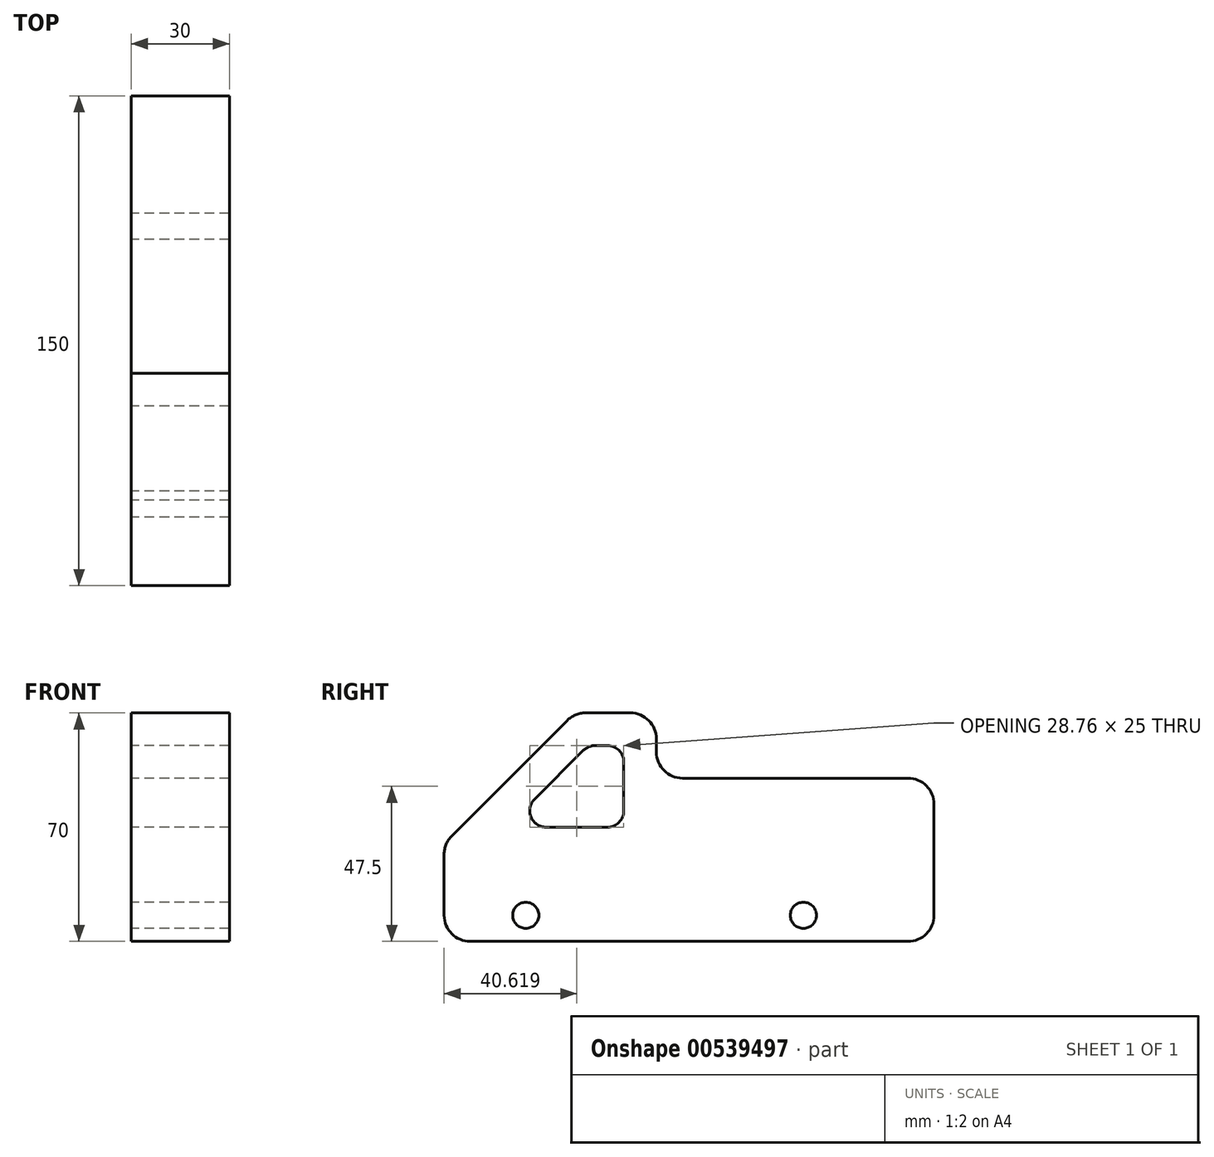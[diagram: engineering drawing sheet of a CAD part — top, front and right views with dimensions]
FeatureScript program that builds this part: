
annotation { "Feature Type Name" : "Feature", "Feature Type Description" : "" }
export const myFeature = defineFeature(function(context is Context, id is Id, definition is map)
    precondition{}
    {
        {
            var Q0;
            Q0=qCreatedBy(makeId("Right.planeOp"),FACE);
            var sketch = newSketch(context, id + "F0", { "sketchPlane" : qUnion([Q0])});
            skLineSegment(sketch, "E0", {"start": v(0, 0) * mm, "end": v(0, 30) * mm});
            skLineSegment(sketch, "E1", {"start": v(0, 30) * mm, "end": v(40, 70) * mm});
            skLineSegment(sketch, "E2", {"start": v(40, 70) * mm, "end": v(65, 70) * mm});
            skLineSegment(sketch, "E3", {"start": v(65, 70) * mm, "end": v(65, 50) * mm});
            skLineSegment(sketch, "E4", {"start": v(65, 50) * mm, "end": v(150, 50) * mm});
            skLineSegment(sketch, "E5", {"start": v(150, 50) * mm, "end": v(150, 0) * mm});
            skLineSegment(sketch, "E6", {"start": v(150, 0) * mm, "end": v(0, 0) * mm});
            skLineSegment(sketch, "E7.0", {"start": v(55, 60) * mm, "end": v(55, 35) * mm});
            skLineSegment(sketch, "E7.1", {"start": v(44.14, 60) * mm, "end": v(55, 60) * mm});
            skLineSegment(sketch, "E7.2", {"start": v(19.14, 35) * mm, "end": v(44.14, 60) * mm});
            skLineSegment(sketch, "E8", {"start": v(19.14, 35) * mm, "end": v(55, 35) * mm});
            skCircle(sketch, "E9", {"center": v(25, 8) * mm, "radius": 4 * mm});
            skCircle(sketch, "E10", {"center": v(110, 8) * mm, "radius": 4 * mm});
            skSolve(sketch);
        }
        {
            var Q0;
            Q0 = qSketchRegion(id + "F0", true);
            extrude(context, id + "F1", {"entities" : qUnion([Q0]), "endBound" : BoundingType.SYMMETRIC, "depth" : 30 * mm, "offsetDistance" : 25 * mm});
        }
        {
            var Q0;
            Q0=makeQuery(id+"F1.opExtrude","SWEPT_EDGE",EDGE,{"disambiguationData":[OSD([sQuery(id+"F0.wireOp",EDGE,"E1"),sQuery(id+"F0.wireOp",EDGE,"E2")])]});
            var Q1;
            Q1=makeQuery(id+"F1.opExtrude","SWEPT_EDGE",EDGE,{"disambiguationData":[OSD([sQuery(id+"F0.wireOp",EDGE,"E0"),sQuery(id+"F0.wireOp",EDGE,"E1")])]});
            var Q2;
            Q2=makeQuery(id+"F1.opExtrude","SWEPT_EDGE",EDGE,{"disambiguationData":[OSD([sQuery(id+"F0.wireOp",EDGE,"E0"),sQuery(id+"F0.wireOp",EDGE,"E6")])]});
            var Q3;
            Q3=makeQuery(id+"F1.opExtrude","SWEPT_EDGE",EDGE,{"disambiguationData":[OSD([sQuery(id+"F0.wireOp",EDGE,"E2"),sQuery(id+"F0.wireOp",EDGE,"E3")])]});
            var Q4;
            Q4=makeQuery(id+"F1.opExtrude","SWEPT_EDGE",EDGE,{"disambiguationData":[OSD([sQuery(id+"F0.wireOp",EDGE,"E3"),sQuery(id+"F0.wireOp",EDGE,"E4")])]});
            var Q5;
            Q5=makeQuery(id+"F1.opExtrude","SWEPT_EDGE",EDGE,{"disambiguationData":[OSD([sQuery(id+"F0.wireOp",EDGE,"E4"),sQuery(id+"F0.wireOp",EDGE,"E5")])]});
            var Q6;
            Q6=makeQuery(id+"F1.opExtrude","SWEPT_EDGE",EDGE,{"disambiguationData":[OSD([sQuery(id+"F0.wireOp",EDGE,"E5"),sQuery(id+"F0.wireOp",EDGE,"E6")])]});
            fillet(context, id + "F2", {"entities" : qUnion([Q0, Q1, Q2, Q3, Q4, Q5, Q6]), "radius" : 8 * mm, "tangentPropagation" : true, "allowEdgeOverflow" : false});
        }
        {
            var Q0;
            Q0=makeQuery(id+"F1.opExtrude","SWEPT_EDGE",EDGE,{"disambiguationData":[OSD([sQuery(id+"F0.wireOp",EDGE,"E7.0"),sQuery(id+"F0.wireOp",EDGE,"E7.1")])]});
            var Q1;
            Q1=makeQuery(id+"F1.opExtrude","SWEPT_EDGE",EDGE,{"disambiguationData":[OSD([sQuery(id+"F0.wireOp",EDGE,"E7.1"),sQuery(id+"F0.wireOp",EDGE,"E7.2")])]});
            var Q2;
            Q2=makeQuery(id+"F1.opExtrude","SWEPT_EDGE",EDGE,{"disambiguationData":[OSD([sQuery(id+"F0.wireOp",EDGE,"E7.2"),sQuery(id+"F0.wireOp",EDGE,"E8")])]});
            var Q3;
            Q3=makeQuery(id+"F1.opExtrude","SWEPT_EDGE",EDGE,{"disambiguationData":[OSD([sQuery(id+"F0.wireOp",EDGE,"E7.0"),sQuery(id+"F0.wireOp",EDGE,"E8")])]});
            fillet(context, id + "F3", {"entities" : qUnion([Q0, Q1, Q2, Q3]), "radius" : 5 * mm, "tangentPropagation" : true, "allowEdgeOverflow" : false});
        }
    });
